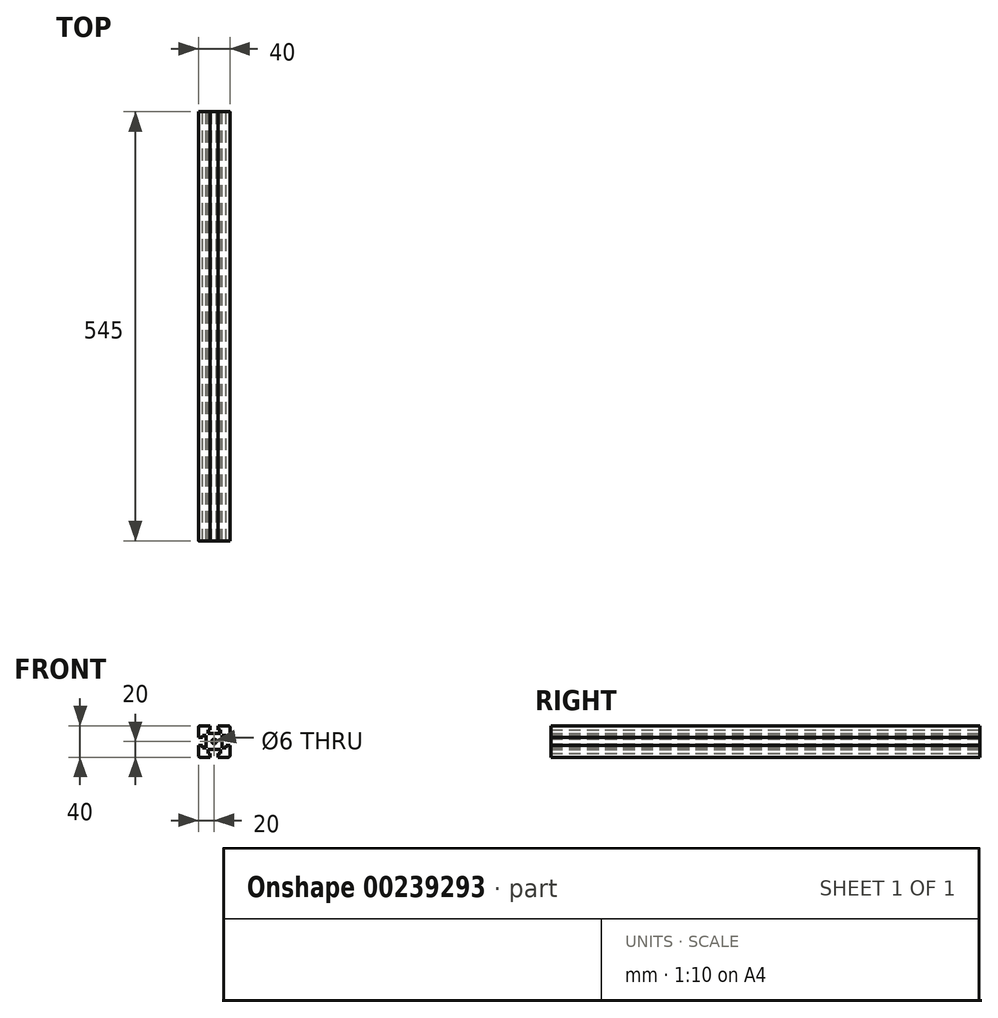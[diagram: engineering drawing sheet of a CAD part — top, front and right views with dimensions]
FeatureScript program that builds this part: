
annotation { "Feature Type Name" : "Feature", "Feature Type Description" : "" }
export const myFeature = defineFeature(function(context is Context, id is Id, definition is map)
    precondition{}
    {
        {
            var Q0;
            Q0=qCreatedBy(makeId("Front.planeOp"),FACE);
            var sketch = newSketch(context, id + "F0", { "sketchPlane" : qUnion([Q0])});
            skLineSegment(sketch, "E0.bottom", {"start": v(-20, 20) * mm, "end": v(20, 20) * mm});
            skLineSegment(sketch, "E0.top", {"start": v(-20, -20) * mm, "end": v(20, -20) * mm});
            skLineSegment(sketch, "E0.left", {"start": v(-20, 20) * mm, "end": v(-20, -20) * mm});
            skLineSegment(sketch, "E0.right", {"start": v(20, 20) * mm, "end": v(20, -20) * mm});
            skSolve(sketch);
        }
        {
            var Q0;
            Q0=makeQuery(id+"F0.imprint","IMPRINT",FACE,{"disambiguationData":[TD([[makeQuery(id+"F0.imprint","IMPRINT",EDGE,{"derivedFrom":sQuery(id+"F0.wireOp",EDGE,"E0.bottom")}),-1.0]])]});
            extrude(context, id + "F1", {"entities" : qUnion([Q0]), "depth" : 545 * mm});
        }
        {
            var Q0;
            Q0=makeQuery(id+"F1.opExtrude","CAP_FACE",FACE,{"disambiguationData":[OSD([sQuery(id+"F0.wireOp",EDGE,"E0.bottom"),sQuery(id+"F0.wireOp",EDGE,"E0.top"),sQuery(id+"F0.wireOp",EDGE,"E0.left"),sQuery(id+"F0.wireOp",EDGE,"E0.right")])],"isStart":true});
            var sketch = newSketch(context, id + "F2", { "sketchPlane" : qUnion([Q0])});
            skLineSegment(sketch, "E1.bottom", {"start": v(-5, 20) * mm, "end": v(5, 20) * mm});
            skLineSegment(sketch, "E1.top", {"start": v(-5, 15) * mm, "end": v(5, 15) * mm});
            skLineSegment(sketch, "E1.left", {"start": v(-5, 20) * mm, "end": v(-5, 15) * mm});
            skLineSegment(sketch, "E1.right", {"start": v(5, 20) * mm, "end": v(5, 15) * mm});
            skLineSegment(sketch, "E2.bottom", {"start": v(-20, 5) * mm, "end": v(-15, 5) * mm});
            skLineSegment(sketch, "E2.top", {"start": v(-20, -5) * mm, "end": v(-15, -5) * mm});
            skLineSegment(sketch, "E2.left", {"start": v(-20, 5) * mm, "end": v(-20, -5) * mm});
            skLineSegment(sketch, "E2.right", {"start": v(-15, 5) * mm, "end": v(-15, -5) * mm});
            skLineSegment(sketch, "E3.bottom", {"start": v(-5, -20) * mm, "end": v(5, -20) * mm});
            skLineSegment(sketch, "E3.top", {"start": v(-5, -15) * mm, "end": v(5, -15) * mm});
            skLineSegment(sketch, "E3.left", {"start": v(-5, -20) * mm, "end": v(-5, -15) * mm});
            skLineSegment(sketch, "E3.right", {"start": v(5, -20) * mm, "end": v(5, -15) * mm});
            skLineSegment(sketch, "E4.bottom", {"start": v(20, 5) * mm, "end": v(15, 5) * mm});
            skLineSegment(sketch, "E4.top", {"start": v(20, -5) * mm, "end": v(15, -5) * mm});
            skLineSegment(sketch, "E4.left", {"start": v(20, 5) * mm, "end": v(20, -5) * mm});
            skLineSegment(sketch, "E4.right", {"start": v(15, 5) * mm, "end": v(15, -5) * mm});
            skLineSegment(sketch, "E5.bottom", {"start": v(-8, 15) * mm, "end": v(8, 15) * mm});
            skLineSegment(sketch, "E5.top", {"start": v(-8, 10) * mm, "end": v(8, 10) * mm});
            skLineSegment(sketch, "E5.left", {"start": v(-8, 15) * mm, "end": v(-8, 10) * mm});
            skLineSegment(sketch, "E5.right", {"start": v(8, 15) * mm, "end": v(8, 10) * mm});
            skLineSegment(sketch, "E6.bottom", {"start": v(-15, 8) * mm, "end": v(-10, 8) * mm});
            skLineSegment(sketch, "E6.top", {"start": v(-15, -8) * mm, "end": v(-10, -8) * mm});
            skLineSegment(sketch, "E6.left", {"start": v(-15, 8) * mm, "end": v(-15, -8) * mm});
            skLineSegment(sketch, "E6.right", {"start": v(-10, 8) * mm, "end": v(-10, -8) * mm});
            skLineSegment(sketch, "E7.bottom", {"start": v(15, 8) * mm, "end": v(10, 8) * mm});
            skLineSegment(sketch, "E7.top", {"start": v(15, -8) * mm, "end": v(10, -8) * mm});
            skLineSegment(sketch, "E7.left", {"start": v(15, 8) * mm, "end": v(15, -8) * mm});
            skLineSegment(sketch, "E7.right", {"start": v(10, 8) * mm, "end": v(10, -8) * mm});
            skLineSegment(sketch, "E8.bottom", {"start": v(-8, -15) * mm, "end": v(8, -15) * mm});
            skLineSegment(sketch, "E8.top", {"start": v(-8, -10) * mm, "end": v(8, -10) * mm});
            skLineSegment(sketch, "E8.left", {"start": v(-8, -15) * mm, "end": v(-8, -10) * mm});
            skLineSegment(sketch, "E8.right", {"start": v(8, -15) * mm, "end": v(8, -10) * mm});
            skCircle(sketch, "E9", {"center": v(0, 0) * mm, "radius": 3 * mm});
            skSolve(sketch);
        }
        {
            var Q0;
            {var subQ0=sQuery(id+"F2.wireOp",EDGE,"E2.bottom");Q0=makeQuery(id+"F2.imprint","IMPRINT",FACE,{"disambiguationData":[TD([[makeQuery(id+"F2.imprint","IMPRINT",EDGE,{"derivedFrom":subQ0}),-1.0]])]});}
            var Q1;
            {var subQ2=sQuery(id+"F2.wireOp",EDGE,"E6.bottom");Q1=makeQuery(id+"F2.imprint","IMPRINT",FACE,{"disambiguationData":[TD([[makeQuery(id+"F2.imprint","IMPRINT",EDGE,{"derivedFrom":subQ2}),-1.0]])]});}
            var Q2;
            Q2=makeQuery(id+"F2.imprint","IMPRINT",FACE,{"disambiguationData":[TD([[makeQuery(id+"F2.imprint","IMPRINT",EDGE,{"derivedFrom":sQuery(id+"F2.wireOp",EDGE,"E5.top")}),1.0]])]});
            var Q3;
            Q3=makeQuery(id+"F2.imprint","IMPRINT",FACE,{"disambiguationData":[TD([[makeQuery(id+"F2.imprint","IMPRINT",EDGE,{"derivedFrom":sQuery(id+"F2.wireOp",EDGE,"E1.bottom")}),1.0]])]});
            var Q4;
            {var subQ4=sQuery(id+"F2.wireOp",EDGE,"E7.bottom");Q4=makeQuery(id+"F2.imprint","IMPRINT",FACE,{"disambiguationData":[TD([[makeQuery(id+"F2.imprint","IMPRINT",EDGE,{"derivedFrom":subQ4}),1.0]])]});}
            var Q5;
            {var subQ0=sQuery(id+"F2.wireOp",EDGE,"E4.bottom");Q5=makeQuery(id+"F2.imprint","IMPRINT",FACE,{"disambiguationData":[TD([[makeQuery(id+"F2.imprint","IMPRINT",EDGE,{"derivedFrom":subQ0}),1.0]])]});}
            var Q6;
            Q6=makeQuery(id+"F2.imprint","IMPRINT",FACE,{"disambiguationData":[TD([[makeQuery(id+"F2.imprint","IMPRINT",EDGE,{"derivedFrom":sQuery(id+"F2.wireOp",EDGE,"E9")}),1.0]])]});
            var Q7;
            Q7=makeQuery(id+"F2.imprint","IMPRINT",FACE,{"disambiguationData":[TD([[makeQuery(id+"F2.imprint","IMPRINT",EDGE,{"derivedFrom":sQuery(id+"F2.wireOp",EDGE,"E8.top")}),-1.0]])]});
            var Q8;
            Q8=makeQuery(id+"F2.imprint","IMPRINT",FACE,{"disambiguationData":[TD([[makeQuery(id+"F2.imprint","IMPRINT",EDGE,{"derivedFrom":sQuery(id+"F2.wireOp",EDGE,"E3.bottom")}),-1.0]])]});
            extrude(context, id + "F3", {"entities" : qUnion([Q0, Q1, Q2, Q3, Q4, Q5, Q6, Q7, Q8]), "operationType" : NewBodyOperationType.REMOVE, "endBound" : BoundingType.THROUGH_ALL, "oppositeDirection" : true, "depth" : 25 * mm});
        }
        {
            var Q0;
            Q0=makeQuery(id+"F1.opExtrude","SWEPT_EDGE",EDGE,{"disambiguationData":[OSD([sQuery(id+"F0.wireOp",EDGE,"E0.bottom"),sQuery(id+"F0.wireOp",EDGE,"E0.right")])]});
            var Q1;
            Q1=makeQuery(id+"F1.opExtrude","SWEPT_EDGE",EDGE,{"disambiguationData":[OSD([sQuery(id+"F0.wireOp",EDGE,"E0.bottom"),sQuery(id+"F0.wireOp",EDGE,"E0.left")])]});
            var Q2;
            Q2=makeQuery(id+"F1.opExtrude","SWEPT_EDGE",EDGE,{"disambiguationData":[OSD([sQuery(id+"F0.wireOp",EDGE,"E0.top"),sQuery(id+"F0.wireOp",EDGE,"E0.right")])]});
            var Q3;
            Q3=makeQuery(id+"F1.opExtrude","SWEPT_EDGE",EDGE,{"disambiguationData":[OSD([sQuery(id+"F0.wireOp",EDGE,"E0.top"),sQuery(id+"F0.wireOp",EDGE,"E0.left")])]});
            fillet(context, id + "F4", {"entities" : qUnion([Q0, Q1, Q2, Q3]), "radius" : 2 * mm, "tangentPropagation" : true, "allowEdgeOverflow" : false});
        }
    });
